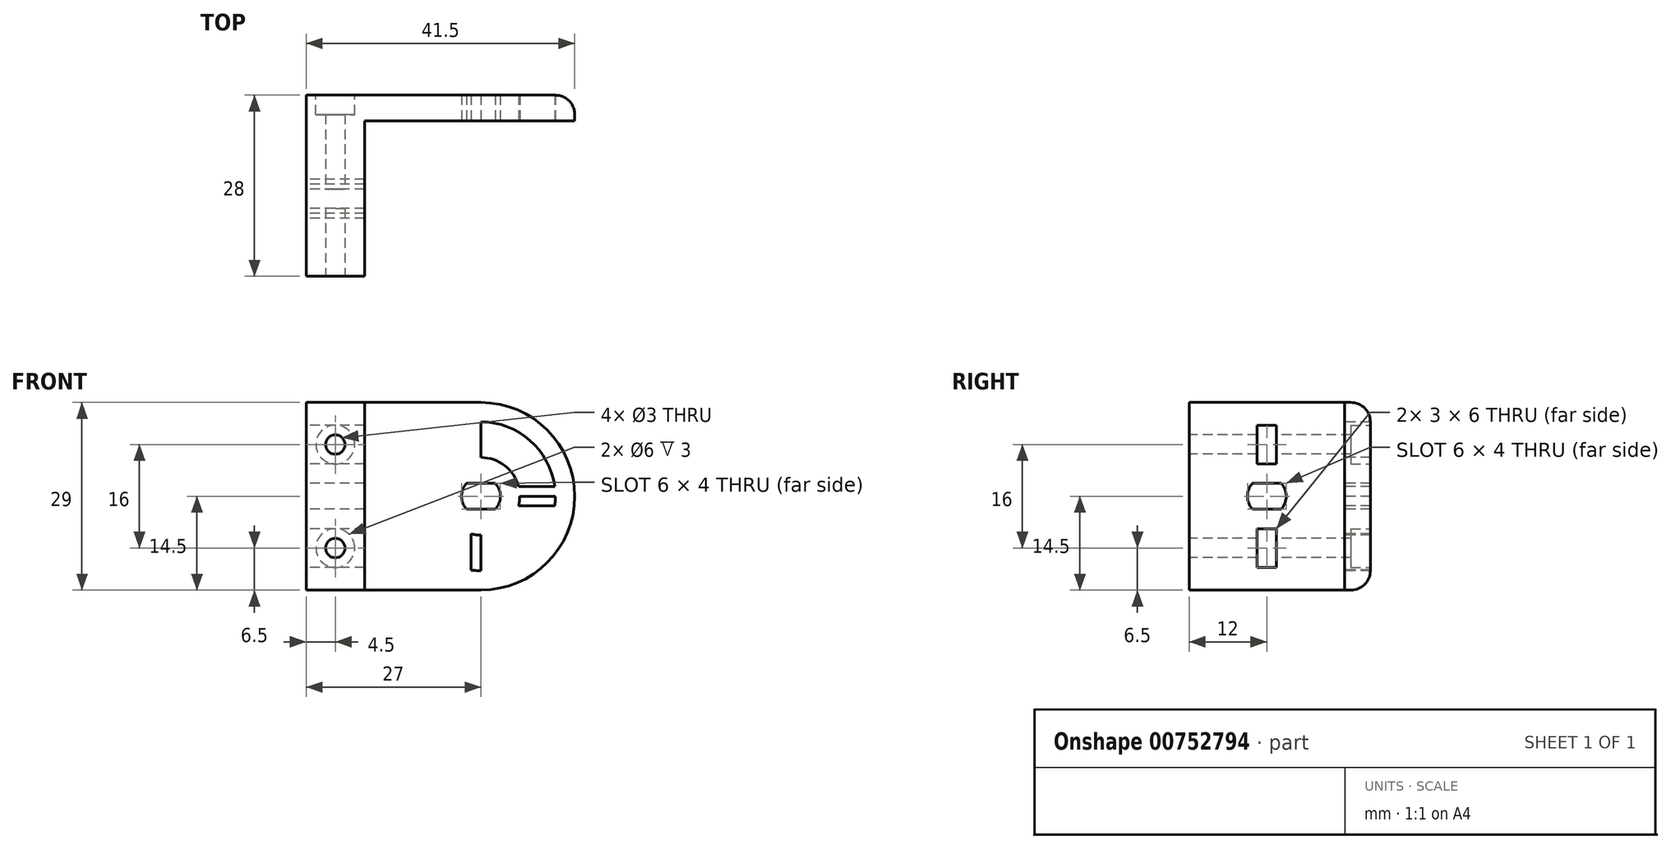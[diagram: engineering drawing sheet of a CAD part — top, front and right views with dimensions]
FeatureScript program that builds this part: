
annotation { "Feature Type Name" : "Feature", "Feature Type Description" : "" }
export const myFeature = defineFeature(function(context is Context, id is Id, definition is map)
    precondition{}
    {
        {
            var Q0;
            Q0=qCreatedBy(makeId("Top.planeOp"),FACE);
            var sketch = newSketch(context, id + "F0", { "sketchPlane" : qUnion([Q0])});
            skLineSegment(sketch, "E0.bottom", {"start": v(-27, -12) * mm, "end": v(-18, -12) * mm});
            skLineSegment(sketch, "E0.top", {"start": v(-27, 16) * mm, "end": v(-18, 16) * mm});
            skLineSegment(sketch, "E0.left", {"start": v(-27, -12) * mm, "end": v(-27, 16) * mm});
            skLineSegment(sketch, "E0.right", {"start": v(-18, -12) * mm, "end": v(-18, 16) * mm});
            skLineSegment(sketch, "E1.bottom", {"start": v(-18, 16) * mm, "end": v(14.5, 16) * mm});
            skLineSegment(sketch, "E1.top", {"start": v(-18, 12) * mm, "end": v(14.5, 12) * mm});
            skLineSegment(sketch, "E1.left", {"start": v(-18, 16) * mm, "end": v(-18, 12) * mm});
            skLineSegment(sketch, "E1.right", {"start": v(14.5, 16) * mm, "end": v(14.5, 12) * mm});
            skSolve(sketch);
        }
        {
            var Q0;
            Q0=makeQuery(id+"F0.imprint","IMPRINT",FACE,{"disambiguationData":[TD([[makeQuery(id+"F0.imprint","IMPRINT",EDGE,{"derivedFrom":sQuery(id+"F0.wireOp",EDGE,"E0.bottom")}),1.0]])]});
            var Q1;
            Q1=makeQuery(id+"F0.imprint","IMPRINT",FACE,{"disambiguationData":[TD([[makeQuery(id+"F0.imprint","IMPRINT",EDGE,{"derivedFrom":sQuery(id+"F0.wireOp",EDGE,"E1.bottom")}),-1.0]])]});
            extrude(context, id + "F1", {"entities" : qUnion([Q0, Q1]), "depth" : 29 * mm, "offsetDistance" : 25 * mm});
        }
        {
            var Q0;
            Q0=makeQuery(id+"F1.opExtrude","CAP_EDGE",EDGE,{"disambiguationData":[OSD([sQuery(id+"F0.wireOp",EDGE,"E1.right")])],"isStart":false});
            var Q1;
            Q1=makeQuery(id+"F1.opExtrude","CAP_EDGE",EDGE,{"disambiguationData":[OSD([sQuery(id+"F0.wireOp",EDGE,"E1.right")])],"isStart":true});
            fillet(context, id + "F2", {"entities" : qUnion([Q0, Q1]), "radius" : 14.5 * mm, "tangentPropagation" : true, "allowEdgeOverflow" : false});
        }
        {
            var Q0;
            Q0=makeQuery(id+"F1.opExtrude","SWEPT_FACE",FACE,{"disambiguationData":[OSD([sQuery(id+"F0.wireOp",EDGE,"E0.bottom")])]});
            var sketch = newSketch(context, id + "F3", { "sketchPlane" : qUnion([Q0])});
            skCircle(sketch, "E2", {"center": v(-22.5, 22.5) * mm, "radius": 1.5 * mm});
            skCircle(sketch, "E3", {"center": v(-22.5, 6.5) * mm, "radius": 1.5 * mm});
            skLineSegment(sketch, "E4", {"start": v(-27, 14.5) * mm, "end": v(-18, 14.5) * mm});
            skSolve(sketch);
        }
        {
            var Q0;
            Q0=makeQuery(id+"F3.imprint","IMPRINT",FACE,{"disambiguationData":[TD([[makeQuery(id+"F3.imprint","IMPRINT",EDGE,{"derivedFrom":sQuery(id+"F3.wireOp",EDGE,"E2")}),1.0]])]});
            var Q1;
            Q1=makeQuery(id+"F3.imprint","IMPRINT",FACE,{"disambiguationData":[TD([[makeQuery(id+"F3.imprint","IMPRINT",EDGE,{"derivedFrom":sQuery(id+"F3.wireOp",EDGE,"E3")}),1.0]])]});
            extrude(context, id + "F4", {"entities" : qUnion([Q0, Q1]), "operationType" : NewBodyOperationType.REMOVE, "endBound" : BoundingType.THROUGH_ALL, "oppositeDirection" : true, "depth" : 25 * mm, "offsetDistance" : 25 * mm});
        }
        {
            var Q0;
            Q0=makeQuery(id+"F1.opExtrude","SWEPT_FACE",FACE,{"disambiguationData":[OSD([sQuery(id+"F0.wireOp",EDGE,"E1.top")])]});
            var sketch = newSketch(context, id + "F5", { "sketchPlane" : qUnion([Q0])});
            skCircle(sketch, "E5", {"center": v(0, 14.5) * mm, "radius": 3 * mm});
            skLineSegment(sketch, "E6.bottom", {"start": v(-2.24, 16.5) * mm, "end": v(2.24, 16.5) * mm});
            skLineSegment(sketch, "E6.top", {"start": v(-2.24, 12.5) * mm, "end": v(2.24, 12.5) * mm});
            skLineSegment(sketch, "E6.left", {"start": v(-2.24, 16.5) * mm, "end": v(-2.24, 12.5) * mm});
            skLineSegment(sketch, "E6.right", {"start": v(2.24, 16.5) * mm, "end": v(2.24, 12.5) * mm});
            skSolve(sketch);
        }
        {
            var Q0;
            Q0=makeQuery(id+"F5.imprint","IMPRINT",FACE,{"disambiguationData":[TD([[makeQuery(id+"F5.imprint","IMPRINT",EDGE,{"derivedFrom":sQuery(id+"F5.wireOp",EDGE,"E6.bottom")}),-1.0]])]});
            var Q1;
            {var subQ0=sQuery(id+"F5.wireOp",EDGE,"E6.left");Q1=makeQuery(id+"F5.imprint","IMPRINT",FACE,{"disambiguationData":[TD([[makeQuery(id+"F5.imprint","IMPRINT",EDGE,{"derivedFrom":subQ0}),-1.0]])]});}
            var Q2;
            {var subQ0=sQuery(id+"F5.wireOp",EDGE,"E6.right");Q2=makeQuery(id+"F5.imprint","IMPRINT",FACE,{"disambiguationData":[TD([[makeQuery(id+"F5.imprint","IMPRINT",EDGE,{"derivedFrom":subQ0}),1.0]])]});}
            extrude(context, id + "F6", {"entities" : qUnion([Q0, Q1, Q2]), "operationType" : NewBodyOperationType.REMOVE, "oppositeDirection" : true, "depth" : 25 * mm, "offsetDistance" : 25 * mm});
        }
        {
            var Q0;
            Q0=makeQuery(id+"F1.opExtrude","SWEPT_FACE",FACE,{"disambiguationData":[OSD([sQuery(id+"F0.wireOp",EDGE,"E0.left")])]});
            var sketch = newSketch(context, id + "F7", { "sketchPlane" : qUnion([Q0])});
            skCircle(sketch, "E7", {"center": v(0, 14.5) * mm, "radius": 3 * mm});
            skPoint(sketch, "E7.centerSnap0", {"position": v(12, 14.5) * mm});
            skLineSegment(sketch, "E8.bottom", {"start": v(-2.24, 16.5) * mm, "end": v(2.24, 16.5) * mm});
            skLineSegment(sketch, "E8.top", {"start": v(-2.24, 12.5) * mm, "end": v(2.24, 12.5) * mm});
            skLineSegment(sketch, "E8.left", {"start": v(-2.24, 16.5) * mm, "end": v(-2.24, 12.5) * mm});
            skLineSegment(sketch, "E8.right", {"start": v(2.24, 16.5) * mm, "end": v(2.24, 12.5) * mm});
            skSolve(sketch);
        }
        {
            var Q0;
            {var subQ0=sQuery(id+"F7.wireOp",EDGE,"E8.left");Q0=makeQuery(id+"F7.imprint","IMPRINT",FACE,{"disambiguationData":[TD([[makeQuery(id+"F7.imprint","IMPRINT",EDGE,{"derivedFrom":subQ0}),-1.0]])]});}
            var Q1;
            {var subQ0=sQuery(id+"F7.wireOp",EDGE,"E8.right");Q1=makeQuery(id+"F7.imprint","IMPRINT",FACE,{"disambiguationData":[TD([[makeQuery(id+"F7.imprint","IMPRINT",EDGE,{"derivedFrom":subQ0}),1.0]])]});}
            var Q2;
            Q2=makeQuery(id+"F7.imprint","IMPRINT",FACE,{"disambiguationData":[TD([[makeQuery(id+"F7.imprint","IMPRINT",EDGE,{"derivedFrom":sQuery(id+"F7.wireOp",EDGE,"E8.bottom")}),-1.0]])]});
            extrude(context, id + "F8", {"entities" : qUnion([Q0, Q1, Q2]), "operationType" : NewBodyOperationType.REMOVE, "oppositeDirection" : true, "depth" : 25 * mm, "offsetDistance" : 25 * mm});
        }
        {
            var Q0;
            Q0=makeQuery(id+"F1.opExtrude","SWEPT_FACE",FACE,{"disambiguationData":[OSD([sQuery(id+"F0.wireOp",EDGE,"E1.top")])]});
            var sketch = newSketch(context, id + "F9", { "sketchPlane" : qUnion([Q0])});
            skCircle(sketch, "E9", {"center": v(0, 14.5) * mm, "radius": 6 * mm});
            skCircle(sketch, "E10", {"center": v(0, 14.5) * mm, "radius": 11.5 * mm});
            skLineSegment(sketch, "E11.bottom", {"start": v(0, 26) * mm, "end": v(-18, 26) * mm});
            skLineSegment(sketch, "E11.top", {"start": v(0, 3) * mm, "end": v(-18, 3) * mm});
            skLineSegment(sketch, "E11.left", {"start": v(0, 26) * mm, "end": v(0, 3) * mm});
            skLineSegment(sketch, "E11.right", {"start": v(-18, 26) * mm, "end": v(-18, 3) * mm});
            skLineSegment(sketch, "E12.bottom", {"start": v(-1.5, 26) * mm, "end": v(1.5, 26) * mm});
            skLineSegment(sketch, "E12.top", {"start": v(-1.5, 3) * mm, "end": v(1.5, 3) * mm});
            skLineSegment(sketch, "E12.left", {"start": v(-1.5, 26) * mm, "end": v(-1.5, 3) * mm});
            skLineSegment(sketch, "E12.right", {"start": v(1.5, 26) * mm, "end": v(1.5, 3) * mm});
            skLineSegment(sketch, "E13.bottom", {"start": v(-18, 16) * mm, "end": v(14.42, 16) * mm});
            skLineSegment(sketch, "E13.top", {"start": v(-18, 13) * mm, "end": v(14.42, 13) * mm});
            skLineSegment(sketch, "E13.left", {"start": v(-18, 16) * mm, "end": v(-18, 13) * mm});
            skLineSegment(sketch, "E13.right", {"start": v(14.42, 16) * mm, "end": v(14.42, 13) * mm});
            skLineSegment(sketch, "E14", {"start": v(0, 14.5) * mm, "end": v(22.72, 14.5) * mm});
            skSolve(sketch);
        }
        {
            var Q0;
            {var subQ0=sQuery(id+"F9.wireOp",EDGE,"E12.left");var subQ1=sQuery(id+"F9.wireOp",EDGE,"E9");var subQ2=makeQuery(id+"F9.imprint","INTERSECT",VERTEX,{"disambiguationData":[OD(0.0)],"derivedFrom":[subQ1,subQ0]});Q0=makeQuery(id+"F9.imprint","IMPRINT",FACE,{"disambiguationData":[TD([[makeQuery(id+"F9.imprint","IMPRINT",EDGE,{"disambiguationData":[TD([[subQ2,-1.0]])],"derivedFrom":subQ1}),-1.0]])]});}
            var Q1;
            {var subQ0=sQuery(id+"F9.wireOp",EDGE,"E13.bottom");var subQ1=sQuery(id+"F9.wireOp",EDGE,"E9");var subQ2=makeQuery(id+"F9.imprint","INTERSECT",VERTEX,{"disambiguationData":[OD(0.0)],"derivedFrom":[subQ1,subQ0]});Q1=makeQuery(id+"F9.imprint","IMPRINT",FACE,{"disambiguationData":[TD([[makeQuery(id+"F9.imprint","IMPRINT",EDGE,{"disambiguationData":[TD([[subQ2,-1.0]])],"derivedFrom":subQ1}),-1.0]])]});}
            var Q2;
            {var subQ0=sQuery(id+"F9.wireOp",EDGE,"E12.right");var subQ1=sQuery(id+"F9.wireOp",EDGE,"E9");var subQ2=makeQuery(id+"F9.imprint","INTERSECT",VERTEX,{"disambiguationData":[OD(1.0)],"derivedFrom":[subQ1,subQ0]});Q2=makeQuery(id+"F9.imprint","IMPRINT",FACE,{"disambiguationData":[TD([[makeQuery(id+"F9.imprint","IMPRINT",EDGE,{"disambiguationData":[TD([[subQ2,-1.0]])],"derivedFrom":subQ1}),-1.0]])]});}
            var Q3;
            {var subQ0=sQuery(id+"F9.wireOp",EDGE,"E13.top");var subQ1=sQuery(id+"F9.wireOp",EDGE,"E9");var subQ2=makeQuery(id+"F9.imprint","INTERSECT",VERTEX,{"disambiguationData":[OD(0.0)],"derivedFrom":[subQ1,subQ0]});Q3=makeQuery(id+"F9.imprint","IMPRINT",FACE,{"disambiguationData":[TD([[makeQuery(id+"F9.imprint","IMPRINT",EDGE,{"disambiguationData":[TD([[subQ2,-1.0]])],"derivedFrom":subQ1}),-1.0]])]});}
            extrude(context, id + "F10", {"entities" : qUnion([Q0, Q1, Q2, Q3]), "operationType" : NewBodyOperationType.REMOVE, "oppositeDirection" : true, "depth" : 25 * mm, "offsetDistance" : 25 * mm});
        }
        {
            var Q0;
            Q0=makeQuery(id+"F2.opFillet","BLEND_EDGE",EDGE,{"blendedFrom":[makeQuery(id+"F1.opExtrude","CAP_EDGE",EDGE,{"disambiguationData":[OSD([sQuery(id+"F0.wireOp",EDGE,"E1.right")])],"isStart":false}),makeQuery(id+"F1.opExtrude","SWEPT_FACE",FACE,{"disambiguationData":[OSD([sQuery(id+"F0.wireOp",EDGE,"E0.top"),sQuery(id+"F0.wireOp",EDGE,"E1.bottom")])]})],"blendedInto":[makeQuery(id+"F1.opExtrude","SWEPT_FACE",FACE,{"disambiguationData":[OSD([sQuery(id+"F0.wireOp",EDGE,"E0.top"),sQuery(id+"F0.wireOp",EDGE,"E1.bottom")])]})]});
            var Q1;
            Q1=makeQuery(id+"F1.opExtrude","CAP_EDGE",EDGE,{"disambiguationData":[OSD([sQuery(id+"F0.wireOp",EDGE,"E0.top"),sQuery(id+"F0.wireOp",EDGE,"E1.bottom")])],"isStart":false});
            var Q2;
            Q2=makeQuery(id+"F1.opExtrude","CAP_EDGE",EDGE,{"disambiguationData":[OSD([sQuery(id+"F0.wireOp",EDGE,"E0.top"),sQuery(id+"F0.wireOp",EDGE,"E1.bottom")])],"isStart":true});
            fillet(context, id + "F11", {"entities" : qUnion([Q0, Q1, Q2]), "radius" : 3 * mm, "tangentPropagation" : true, "allowEdgeOverflow" : false});
        }
        {
            var Q0;
            Q0=makeQuery(id+"F1.opExtrude","SWEPT_FACE",FACE,{"disambiguationData":[OSD([sQuery(id+"F0.wireOp",EDGE,"E0.left")])]});
            var sketch = newSketch(context, id + "F12", { "sketchPlane" : qUnion([Q0])});
            skLineSegment(sketch, "E15.0", {"start": v(12, 24) * mm, "end": v(12, 21) * mm});
            skLineSegment(sketch, "E16.0", {"start": v(12, 8) * mm, "end": v(12, 5) * mm});
            skLineSegment(sketch, "E17", {"start": v(12, 5) * mm, "end": v(-16, 5) * mm});
            skLineSegment(sketch, "E18", {"start": v(-16, 8) * mm, "end": v(12, 8) * mm});
            skLineSegment(sketch, "E19", {"start": v(-16, 24) * mm, "end": v(12, 24) * mm});
            skLineSegment(sketch, "E20", {"start": v(12, 21) * mm, "end": v(-16, 21) * mm});
            skLineSegment(sketch, "E21.bottom", {"start": v(-1.5, 25.5) * mm, "end": v(1.5, 25.5) * mm});
            skLineSegment(sketch, "E21.top", {"start": v(-1.5, 19.5) * mm, "end": v(1.5, 19.5) * mm});
            skLineSegment(sketch, "E21.left", {"start": v(-1.5, 25.5) * mm, "end": v(-1.5, 19.5) * mm});
            skLineSegment(sketch, "E21.right", {"start": v(1.5, 25.5) * mm, "end": v(1.5, 19.5) * mm});
            skLineSegment(sketch, "E22.0.1.0", {"start": v(1.5, 9.5) * mm, "end": v(1.5, 3.5) * mm});
            skLineSegment(sketch, "E22.0.1.1", {"start": v(-1.5, 9.5) * mm, "end": v(-1.5, 3.5) * mm});
            skLineSegment(sketch, "E22.0.1.2", {"start": v(-1.5, 9.5) * mm, "end": v(1.5, 9.5) * mm});
            skLineSegment(sketch, "E22.0.1.3", {"start": v(-1.5, 3.5) * mm, "end": v(1.5, 3.5) * mm});
            skLineSegment(sketch, "E22.direction1", {"start": v(1.5, 19.5) * mm, "end": v(26.5, 19.5) * mm, "construction": true});
            skLineSegment(sketch, "E22.direction2", {"start": v(1.5, 19.5) * mm, "end": v(1.5, 3.5) * mm, "construction": true});
            skSolve(sketch);
        }
        {
            var Q0;
            {var subQ5=sQuery(id+"F12.wireOp",EDGE,"E21.bottom");Q0=makeQuery(id+"F12.imprint","IMPRINT",FACE,{"disambiguationData":[TD([[makeQuery(id+"F12.imprint","IMPRINT",EDGE,{"derivedFrom":subQ5}),-1.0]])]});}
            var Q1;
            {var subQ0=sQuery(id+"F12.wireOp",EDGE,"E21.left");var subQ1=sQuery(id+"F12.wireOp",EDGE,"E19");var subQ2=makeQuery(id+"F12.imprint","INTERSECT",VERTEX,{"derivedFrom":[subQ1,subQ0]});Q1=makeQuery(id+"F12.imprint","IMPRINT",FACE,{"disambiguationData":[TD([[makeQuery(id+"F12.imprint","IMPRINT",EDGE,{"disambiguationData":[TD([[subQ2,-1.0]])],"derivedFrom":subQ1}),-1.0]])]});}
            var Q2;
            {var subQ5=sQuery(id+"F12.wireOp",EDGE,"E21.top");Q2=makeQuery(id+"F12.imprint","IMPRINT",FACE,{"disambiguationData":[TD([[makeQuery(id+"F12.imprint","IMPRINT",EDGE,{"derivedFrom":subQ5}),1.0]])]});}
            var Q3;
            {var subQ5=sQuery(id+"F12.wireOp",EDGE,"E22.0.1.2");Q3=makeQuery(id+"F12.imprint","IMPRINT",FACE,{"disambiguationData":[TD([[makeQuery(id+"F12.imprint","IMPRINT",EDGE,{"derivedFrom":subQ5}),-1.0]])]});}
            var Q4;
            {var subQ0=sQuery(id+"F12.wireOp",EDGE,"E22.0.1.0");var subQ1=sQuery(id+"F12.wireOp",EDGE,"E17");var subQ2=makeQuery(id+"F12.imprint","INTERSECT",VERTEX,{"derivedFrom":[subQ1,subQ0]});Q4=makeQuery(id+"F12.imprint","IMPRINT",FACE,{"disambiguationData":[TD([[makeQuery(id+"F12.imprint","IMPRINT",EDGE,{"disambiguationData":[TD([[subQ2,-1.0]])],"derivedFrom":subQ1}),-1.0]])]});}
            var Q5;
            {var subQ5=sQuery(id+"F12.wireOp",EDGE,"E22.0.1.3");Q5=makeQuery(id+"F12.imprint","IMPRINT",FACE,{"disambiguationData":[TD([[makeQuery(id+"F12.imprint","IMPRINT",EDGE,{"derivedFrom":subQ5}),1.0]])]});}
            extrude(context, id + "F13", {"entities" : qUnion([Q0, Q1, Q2, Q3, Q4, Q5]), "operationType" : NewBodyOperationType.REMOVE, "oppositeDirection" : true, "depth" : 25 * mm, "offsetDistance" : 25 * mm});
        }
        {
            var Q0;
            Q0=makeQuery(id+"F1.opExtrude","SWEPT_FACE",FACE,{"disambiguationData":[OSD([sQuery(id+"F0.wireOp",EDGE,"E0.top"),sQuery(id+"F0.wireOp",EDGE,"E1.bottom")])]});
            var sketch = newSketch(context, id + "F14", { "sketchPlane" : qUnion([Q0])});
            skCircle(sketch, "E23", {"center": v(22.5, 22.5) * mm, "radius": 3 * mm});
            skCircle(sketch, "E24", {"center": v(22.5, 6.5) * mm, "radius": 3 * mm});
            skSolve(sketch);
        }
        {
            var Q0;
            Q0=makeQuery(id+"F14.imprint","IMPRINT",FACE,{"disambiguationData":[TD([[makeQuery(id+"F14.imprint","IMPRINT",EDGE,{"derivedFrom":sQuery(id+"F14.wireOp",EDGE,"E23")}),1.0]])]});
            var Q1;
            Q1=makeQuery(id+"F14.imprint","IMPRINT",FACE,{"disambiguationData":[TD([[makeQuery(id+"F14.imprint","IMPRINT",EDGE,{"derivedFrom":sQuery(id+"F14.wireOp",EDGE,"E24")}),1.0]])]});
            extrude(context, id + "F15", {"entities" : qUnion([Q0, Q1]), "operationType" : NewBodyOperationType.REMOVE, "oppositeDirection" : true, "depth" : 3 * mm, "offsetDistance" : 25 * mm});
        }
    });
